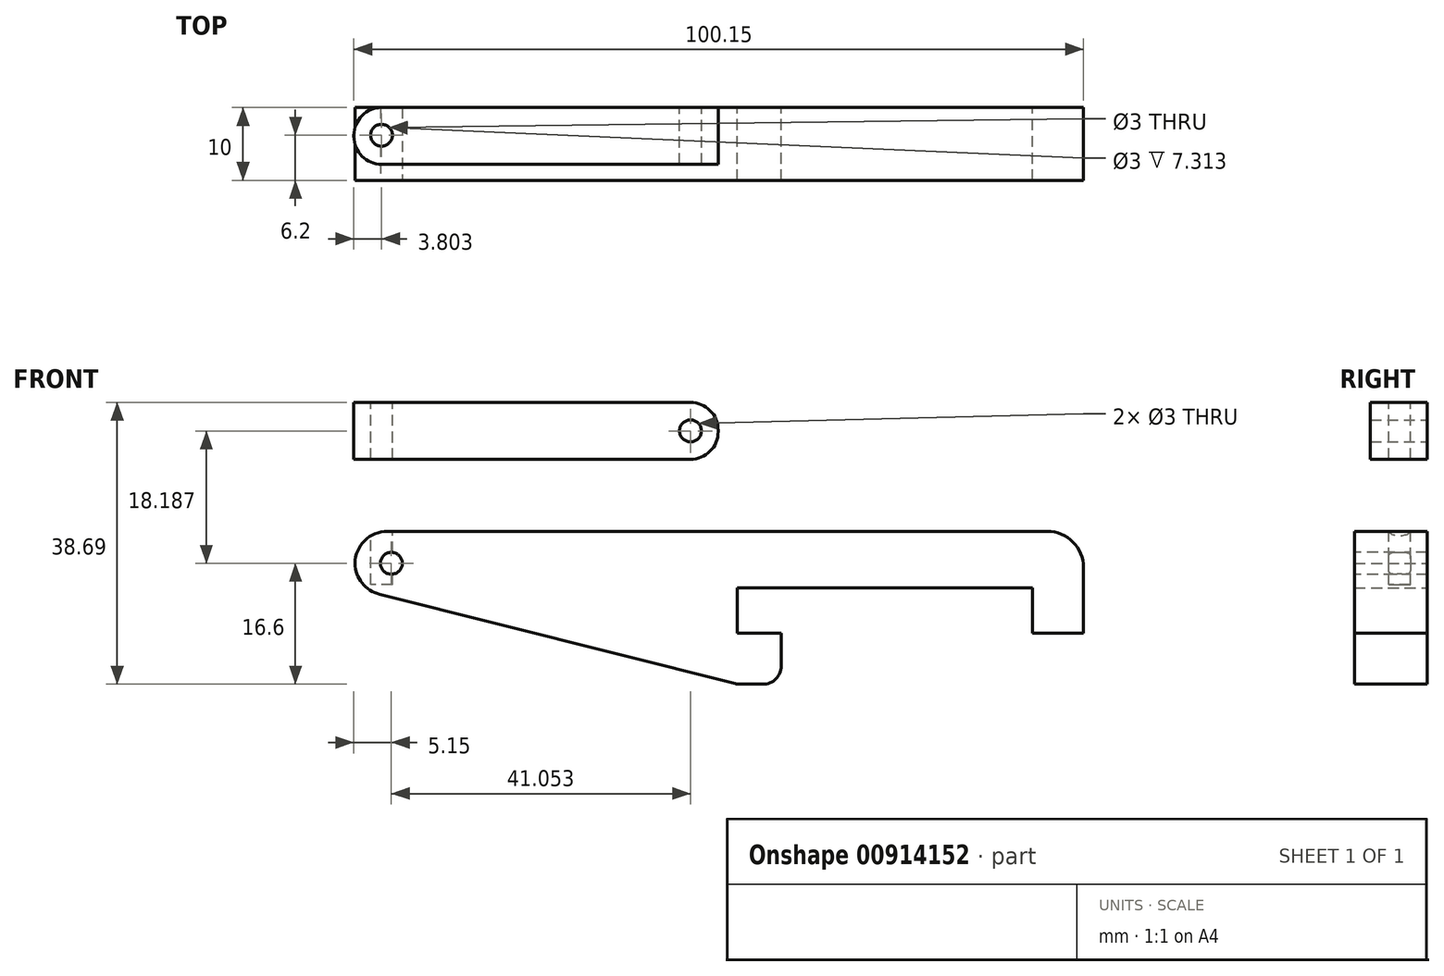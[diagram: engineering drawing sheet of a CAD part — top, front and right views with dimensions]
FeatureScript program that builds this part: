
annotation { "Feature Type Name" : "Feature", "Feature Type Description" : "" }
export const myFeature = defineFeature(function(context is Context, id is Id, definition is map)
    precondition{}
    {
        {
            var Q0;
            Q0=qCreatedBy(makeId("Front.planeOp"),FACE);
            var sketch = newSketch(context, id + "F0", { "sketchPlane" : qUnion([Q0])});
            skLineSegment(sketch, "E0.bottom", {"start": v(0, 0) * mm, "end": v(-40.5, 0) * mm});
            skLineSegment(sketch, "E0.top", {"start": v(-34.5, -6.2) * mm, "end": v(-40.5, -6.2) * mm});
            skLineSegment(sketch, "E0.left", {"start": v(0, 0) * mm, "end": v(0, -6.2) * mm});
            skLineSegment(sketch, "E0.right", {"start": v(-40.5, 0) * mm, "end": v(-40.5, -6.2) * mm});
            skLineSegment(sketch, "E1", {"start": v(0, -6.2) * mm, "end": v(7, -6.2) * mm});
            skLineSegment(sketch, "E2", {"start": v(7, -6.2) * mm, "end": v(7, 7.8) * mm});
            skLineSegment(sketch, "E3", {"start": v(7, 7.8) * mm, "end": v(-93, 7.8) * mm});
            skLineSegment(sketch, "E4", {"start": v(-40.5, -6.2) * mm, "end": v(-34.5, -6.2) * mm});
            skLineSegment(sketch, "E5", {"start": v(-34.5, -6.2) * mm, "end": v(-34.5, -13.2) * mm});
            skLineSegment(sketch, "E6", {"start": v(-34.5, -13.2) * mm, "end": v(-40.5, -13.2) * mm});
            skLineSegment(sketch, "E7", {"start": v(-93, 7.8) * mm, "end": v(-93, 0) * mm});
            skLineSegment(sketch, "E8", {"start": v(-93, 0) * mm, "end": v(-40.5, -13.2) * mm});
            skSolve(sketch);
        }
        {
            var Q0;
            Q0=makeQuery(id+"F0.imprint","IMPRINT",FACE,{"disambiguationData":[TD([[makeQuery(id+"F0.imprint","IMPRINT",EDGE,{"derivedFrom":sQuery(id+"F0.wireOp",EDGE,"E0.bottom")}),-1.0]])]});
            extrude(context, id + "F1", {"entities" : qUnion([Q0]), "depth" : 10 * mm, "offsetDistance" : 25 * mm});
        }
        {
            var Q0;
            Q0=makeQuery(id+"F1.opExtrude","SWEPT_EDGE",EDGE,{"disambiguationData":[OSD([sQuery(id+"F0.wireOp",EDGE,"E2"),sQuery(id+"F0.wireOp",EDGE,"E3")])]});
            fillet(context, id + "F2", {"entities" : qUnion([Q0]), "radius" : 5 * mm, "tangentPropagation" : true, "allowEdgeOverflow" : false});
        }
        {
            var Q0;
            Q0=makeQuery(id+"F1.opExtrude","SWEPT_EDGE",EDGE,{"disambiguationData":[OSD([sQuery(id+"F0.wireOp",EDGE,"E5"),sQuery(id+"F0.wireOp",EDGE,"E6")])]});
            var Q1;
            Q1=makeQuery(id+"F1.opExtrude","SWEPT_EDGE",EDGE,{"disambiguationData":[OSD([sQuery(id+"F0.wireOp",EDGE,"E6"),sQuery(id+"F0.wireOp",EDGE,"04XB2HVS-MTA2-xwZm-yKOP-dUufRqHIiRfc")])]});
            fillet(context, id + "F3", {"entities" : qUnion([Q0, Q1]), "radius" : 2.5 * mm, "tangentPropagation" : true, "allowEdgeOverflow" : false});
        }
        {
            var Q0;
            Q0=makeQuery(id+"F1.opExtrude","SWEPT_EDGE",EDGE,{"disambiguationData":[OSD([sQuery(id+"F0.wireOp",EDGE,"E7"),sQuery(id+"F0.wireOp",EDGE,"E8")])]});
            var Q1;
            Q1=makeQuery(id+"F1.opExtrude","SWEPT_EDGE",EDGE,{"disambiguationData":[OSD([sQuery(id+"F0.wireOp",EDGE,"E3"),sQuery(id+"F0.wireOp",EDGE,"E7")])]});
            fillet(context, id + "F4", {"entities" : qUnion([Q0, Q1]), "radius" : 4.5 * mm, "tangentPropagation" : true, "allowEdgeOverflow" : false});
        }
        {
            var Q0;
            Q0=makeQuery(id+"F1.opExtrude","CAP_FACE",FACE,{"disambiguationData":[OSD([sQuery(id+"F0.wireOp",EDGE,"E0.bottom"),sQuery(id+"F0.wireOp",EDGE,"E0.left"),sQuery(id+"F0.wireOp",EDGE,"E0.right"),sQuery(id+"F0.wireOp",EDGE,"E1"),sQuery(id+"F0.wireOp",EDGE,"E2"),sQuery(id+"F0.wireOp",EDGE,"E3"),sQuery(id+"F0.wireOp",EDGE,"E4"),sQuery(id+"F0.wireOp",EDGE,"E5"),sQuery(id+"F0.wireOp",EDGE,"E6"),sQuery(id+"F0.wireOp",EDGE,"E7"),sQuery(id+"F0.wireOp",EDGE,"E8")])],"isStart":false});
            var sketch = newSketch(context, id + "F5", { "sketchPlane" : qUnion([Q0])});
            skCircle(sketch, "E9", {"center": v(-88, 3.4) * mm, "radius": 1.5 * mm});
            skSolve(sketch);
        }
        {
            var Q0;
            Q0=makeQuery(id+"F5.imprint","IMPRINT",FACE,{"disambiguationData":[TD([[makeQuery(id+"F5.imprint","IMPRINT",EDGE,{"derivedFrom":sQuery(id+"F5.wireOp",EDGE,"E9")}),1.0]])]});
            extrude(context, id + "F6", {"entities" : qUnion([Q0]), "operationType" : NewBodyOperationType.REMOVE, "oppositeDirection" : true, "depth" : 25 * mm, "offsetDistance" : 25 * mm});
        }
        {
            var Q0;
            Q0=qCreatedBy(makeId("Front.planeOp"),FACE);
            var sketch = newSketch(context, id + "F7", { "sketchPlane" : qUnion([Q0])});
            skLineSegment(sketch, "E10.bottom", {"start": v(-43.15, 17.69) * mm, "end": v(-93.15, 17.69) * mm});
            skLineSegment(sketch, "E10.top", {"start": v(-43.15, 25.49) * mm, "end": v(-93.15, 25.49) * mm});
            skLineSegment(sketch, "E10.left", {"start": v(-43.15, 17.69) * mm, "end": v(-43.15, 25.49) * mm});
            skLineSegment(sketch, "E10.right", {"start": v(-93.15, 17.69) * mm, "end": v(-93.15, 25.49) * mm});
            skCircle(sketch, "E11", {"center": v(-46.95, 21.59) * mm, "radius": 1.5 * mm});
            skPoint(sketch, "E11.centerSnap0", {"position": v(-43.15, 21.59) * mm});
            skSolve(sketch);
        }
        {
            var Q0;
            Q0=makeQuery(id+"F7.imprint","IMPRINT",FACE,{"disambiguationData":[TD([[makeQuery(id+"F7.imprint","IMPRINT",EDGE,{"derivedFrom":sQuery(id+"F7.wireOp",EDGE,"E10.bottom")}),-1.0]])]});
            extrude(context, id + "F8", {"entities" : qUnion([Q0]), "depth" : 7.8 * mm, "offsetDistance" : 25 * mm});
        }
        {
            var Q0;
            Q0=makeQuery(id+"F8.opExtrude","SWEPT_EDGE",EDGE,{"disambiguationData":[OSD([sQuery(id+"F7.wireOp",EDGE,"E10.top"),sQuery(id+"F7.wireOp",EDGE,"E10.left")])]});
            var Q1;
            Q1=makeQuery(id+"F8.opExtrude","SWEPT_EDGE",EDGE,{"disambiguationData":[OSD([sQuery(id+"F7.wireOp",EDGE,"E10.bottom"),sQuery(id+"F7.wireOp",EDGE,"E10.left")])]});
            var Q2;
            Q2=makeQuery(id+"F8.opExtrude","CAP_EDGE",EDGE,{"disambiguationData":[OSD([sQuery(id+"F7.wireOp",EDGE,"E10.right")])],"isStart":false});
            var Q3;
            Q3=makeQuery(id+"F8.opExtrude","CAP_EDGE",EDGE,{"disambiguationData":[OSD([sQuery(id+"F7.wireOp",EDGE,"E10.right")])],"isStart":true});
            fillet(context, id + "F9", {"entities" : qUnion([Q0, Q1, Q2, Q3]), "radius" : 3.8 * mm, "tangentPropagation" : true, "allowEdgeOverflow" : false});
        }
        {
            var Q0;
            Q0=makeQuery(id+"F8.opExtrude","SWEPT_FACE",FACE,{"disambiguationData":[OSD([sQuery(id+"F7.wireOp",EDGE,"E10.top")])]});
            var sketch = newSketch(context, id + "F10", { "sketchPlane" : qUnion([Q0])});
            skCircle(sketch, "E12", {"center": v(-89.35, -3.8) * mm, "radius": 1.5 * mm});
            skSolve(sketch);
        }
        {
            var Q0;
            Q0=makeQuery(id+"F10.imprint","IMPRINT",FACE,{"disambiguationData":[TD([[makeQuery(id+"F10.imprint","IMPRINT",EDGE,{"derivedFrom":sQuery(id+"F10.wireOp",EDGE,"E12")}),1.0]])]});
            extrude(context, id + "F11", {"entities" : qUnion([Q0]), "operationType" : NewBodyOperationType.REMOVE, "oppositeDirection" : true, "depth" : 25 * mm, "offsetDistance" : 25 * mm});
        }
    });
